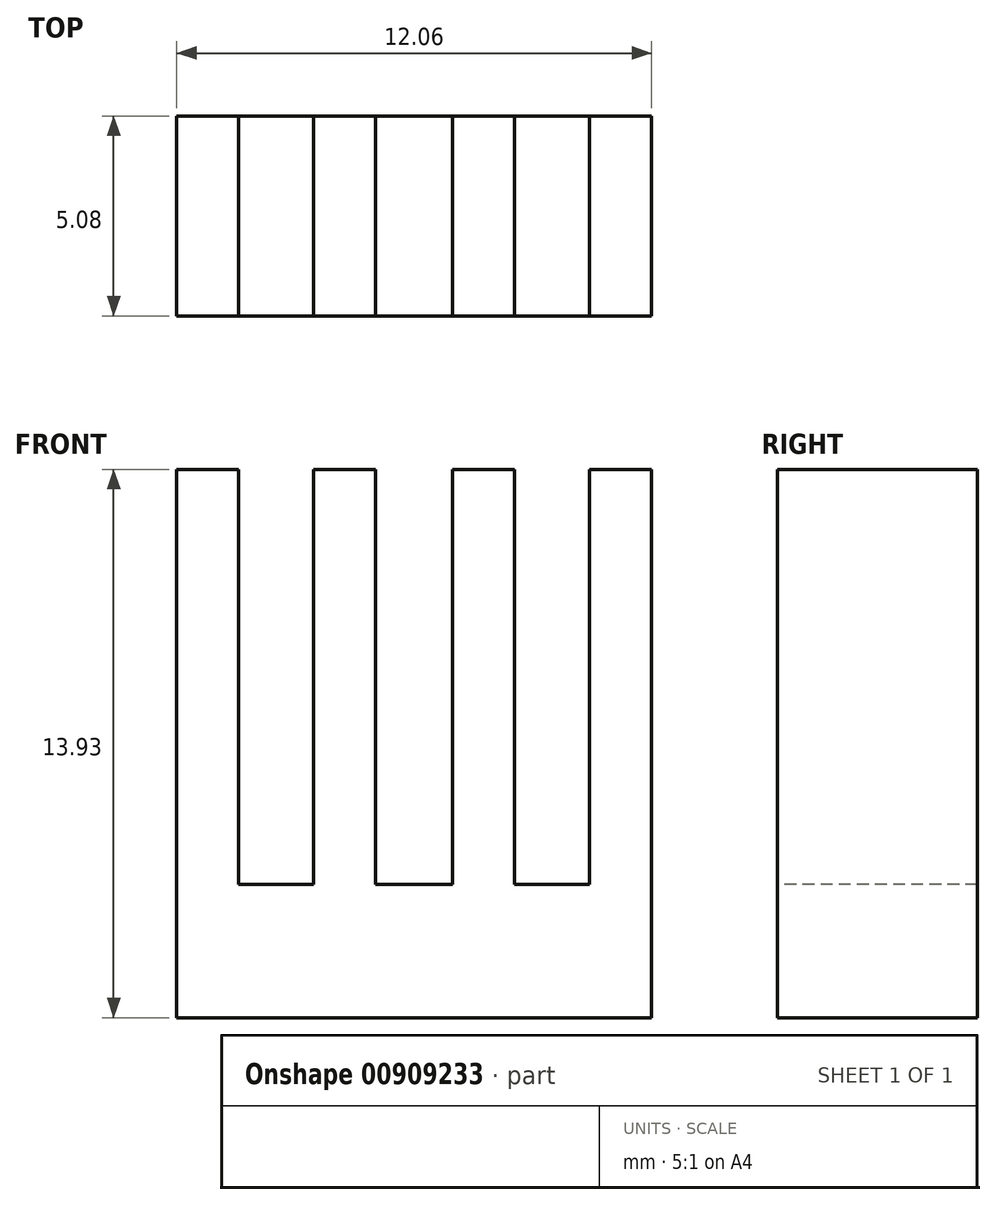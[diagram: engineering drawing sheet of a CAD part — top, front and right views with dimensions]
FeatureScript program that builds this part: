
annotation { "Feature Type Name" : "Feature", "Feature Type Description" : "" }
export const myFeature = defineFeature(function(context is Context, id is Id, definition is map)
    precondition{}
    {
        {
            var Q0;
            Q0=qCreatedBy(makeId("Top.planeOp"),FACE);
            var sketch = newSketch(context, id + "F0", { "sketchPlane" : qUnion([Q0])});
            skLineSegment(sketch, "E0.bottom", {"start": v(-6.03, 2.54) * mm, "end": v(6.03, 2.54) * mm});
            skLineSegment(sketch, "E0.top", {"start": v(-6.03, -2.54) * mm, "end": v(6.03, -2.54) * mm});
            skLineSegment(sketch, "E0.left", {"start": v(-6.03, 2.54) * mm, "end": v(-6.03, -2.54) * mm});
            skLineSegment(sketch, "E0.right", {"start": v(6.03, 2.54) * mm, "end": v(6.03, -2.54) * mm});
            skPoint(sketch, "E0.middle", {"position": v(0, 0) * mm});
            skSolve(sketch);
        }
        {
            var Q0;
            Q0 = qSketchRegion(id + "F0", true);
            extrude(context, id + "F1", {"entities" : qUnion([Q0]), "depth" : 3.4 * mm, "offsetDistance" : 25.4 * mm});
        }
        {
            var Q0;
            Q0=makeQuery(id+"F1.opExtrude","CAP_FACE",FACE,{"disambiguationData":[OSD([sQuery(id+"F0.wireOp",EDGE,"E0.bottom"),sQuery(id+"F0.wireOp",EDGE,"E0.top"),sQuery(id+"F0.wireOp",EDGE,"E0.left"),sQuery(id+"F0.wireOp",EDGE,"E0.right")])],"isStart":false});
            var sketch = newSketch(context, id + "F2", { "sketchPlane" : qUnion([Q0])});
            skLineSegment(sketch, "E1.bottom", {"start": v(6.03, 2.54) * mm, "end": v(4.46, 2.54) * mm});
            skLineSegment(sketch, "E1.top", {"start": v(6.03, -2.54) * mm, "end": v(4.46, -2.54) * mm});
            skLineSegment(sketch, "E1.left", {"start": v(6.03, 2.54) * mm, "end": v(6.03, -2.54) * mm});
            skLineSegment(sketch, "E1.right", {"start": v(4.46, 2.54) * mm, "end": v(4.46, -2.54) * mm});
            skLineSegment(sketch, "E2.bottom", {"start": v(-6.03, 2.54) * mm, "end": v(-4.46, 2.54) * mm});
            skLineSegment(sketch, "E2.top", {"start": v(-6.03, -2.54) * mm, "end": v(-4.46, -2.54) * mm});
            skLineSegment(sketch, "E2.left", {"start": v(-6.03, 2.54) * mm, "end": v(-6.03, -2.54) * mm});
            skLineSegment(sketch, "E2.right", {"start": v(-4.46, 2.54) * mm, "end": v(-4.46, -2.54) * mm});
            skLineSegment(sketch, "E3.bottom", {"start": v(0.98, 2.54) * mm, "end": v(2.55, 2.54) * mm});
            skLineSegment(sketch, "E3.top", {"start": v(0.98, -2.54) * mm, "end": v(2.55, -2.54) * mm});
            skLineSegment(sketch, "E3.left", {"start": v(0.98, 2.54) * mm, "end": v(0.98, -2.54) * mm});
            skLineSegment(sketch, "E3.right", {"start": v(2.55, 2.54) * mm, "end": v(2.55, -2.54) * mm});
            skLineSegment(sketch, "E4.bottom", {"start": v(-2.55, 2.54) * mm, "end": v(-0.98, 2.54) * mm});
            skLineSegment(sketch, "E4.top", {"start": v(-2.55, -2.54) * mm, "end": v(-0.98, -2.54) * mm});
            skLineSegment(sketch, "E4.left", {"start": v(-2.55, 2.54) * mm, "end": v(-2.55, -2.54) * mm});
            skLineSegment(sketch, "E4.right", {"start": v(-0.98, 2.54) * mm, "end": v(-0.98, -2.54) * mm});
            skSolve(sketch);
        }
        {
            var Q0;
            Q0 = qSketchRegion(id + "F2", true);
            extrude(context, id + "F3", {"entities" : qUnion([Q0]), "operationType" : NewBodyOperationType.ADD, "depth" : 10.54 * mm, "offsetDistance" : 25.4 * mm});
        }
    });
